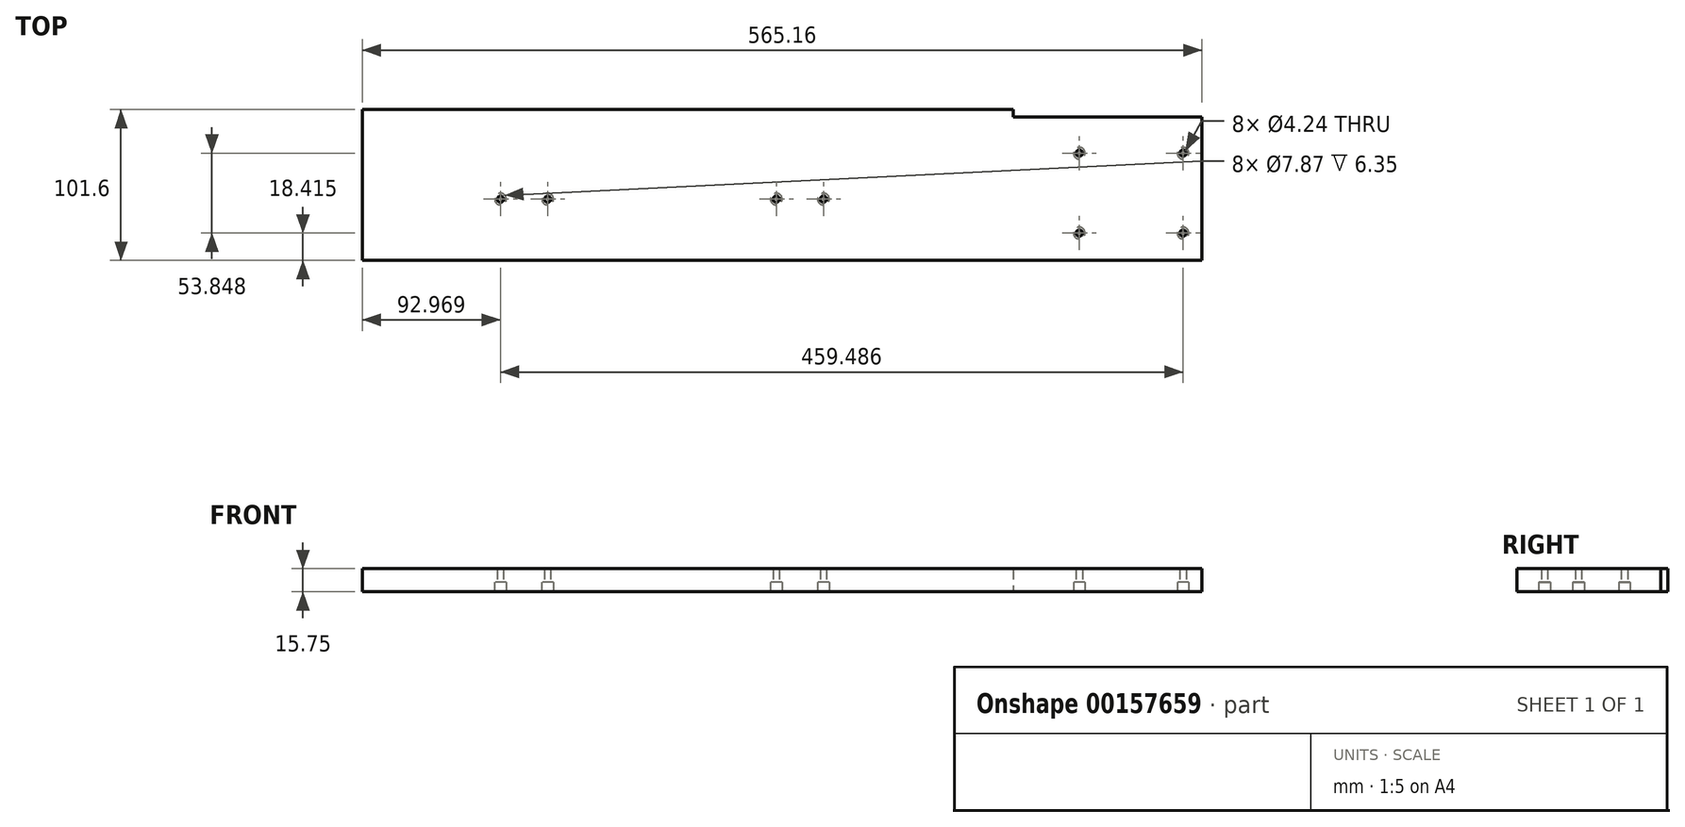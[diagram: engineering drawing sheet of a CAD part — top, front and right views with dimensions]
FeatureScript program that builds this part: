
annotation { "Feature Type Name" : "Feature", "Feature Type Description" : "" }
export const myFeature = defineFeature(function(context is Context, id is Id, definition is map)
    precondition{}
    {
        {
            var Q0;
            Q0=qCreatedBy(makeId("Top.planeOp"),FACE);
            var sketch = newSketch(context, id + "F0", { "sketchPlane" : qUnion([Q0])});
            skLineSegment(sketch, "E0.bottom", {"start": v(282.58, -50.8) * mm, "end": v(-282.58, -50.8) * mm});
            skLineSegment(sketch, "E0.top", {"start": v(155.58, 50.8) * mm, "end": v(-282.58, 50.8) * mm});
            skLineSegment(sketch, "E0.left", {"start": v(282.58, -50.8) * mm, "end": v(282.58, 45.97) * mm});
            skLineSegment(sketch, "E0.right", {"start": v(-282.58, -50.8) * mm, "end": v(-282.58, 50.8) * mm});
            skPoint(sketch, "E0.middle", {"position": v(0, 0) * mm});
            skLineSegment(sketch, "E1.bottom", {"start": v(269.88, -32.38) * mm, "end": v(200.03, -32.38) * mm, "construction": true});
            skLineSegment(sketch, "E1.top", {"start": v(269.88, 21.46) * mm, "end": v(200.03, 21.46) * mm, "construction": true});
            skLineSegment(sketch, "E1.left", {"start": v(269.88, -32.38) * mm, "end": v(269.88, 21.46) * mm, "construction": true});
            skLineSegment(sketch, "E1.right", {"start": v(200.03, -32.38) * mm, "end": v(200.03, 21.46) * mm, "construction": true});
            skPoint(sketch, "E1.middle", {"position": v(234.95, -5.46) * mm});
            skCircle(sketch, "E2", {"center": v(200.03, 21.46) * mm, "radius": 2.12 * mm});
            skCircle(sketch, "E3", {"center": v(269.88, 21.46) * mm, "radius": 2.12 * mm});
            skCircle(sketch, "E4", {"center": v(200.03, -32.38) * mm, "radius": 2.12 * mm});
            skCircle(sketch, "E5", {"center": v(269.88, -32.38) * mm, "radius": 2.12 * mm});
            skCircle(sketch, "E6", {"center": v(200.03, 21.46) * mm, "radius": 3.94 * mm});
            skCircle(sketch, "E7", {"center": v(269.88, 21.46) * mm, "radius": 3.94 * mm});
            skCircle(sketch, "E8", {"center": v(269.88, -32.38) * mm, "radius": 3.94 * mm});
            skCircle(sketch, "E9", {"center": v(200.03, -32.38) * mm, "radius": 3.94 * mm});
            skCircle(sketch, "E10", {"center": v(27.81, -9.52) * mm, "radius": 2.12 * mm});
            skCircle(sketch, "E11", {"center": v(-3.94, -9.53) * mm, "radius": 2.12 * mm});
            skCircle(sketch, "E12", {"center": v(-157.86, -9.53) * mm, "radius": 2.12 * mm});
            skCircle(sketch, "E13", {"center": v(-189.61, -9.53) * mm, "radius": 2.12 * mm});
            skCircle(sketch, "E14", {"center": v(27.81, -9.52) * mm, "radius": 3.94 * mm});
            skCircle(sketch, "E15", {"center": v(-3.94, -9.53) * mm, "radius": 3.94 * mm});
            skCircle(sketch, "E16", {"center": v(-157.86, -9.53) * mm, "radius": 3.94 * mm});
            skCircle(sketch, "E17", {"center": v(-189.61, -9.53) * mm, "radius": 3.94 * mm});
            skLineSegment(sketch, "E18.top", {"start": v(282.58, 45.97) * mm, "end": v(155.58, 45.97) * mm, "construction": true});
            skLineSegment(sketch, "E18.right", {"start": v(155.58, 50.8) * mm, "end": v(155.58, 45.97) * mm, "construction": true});
            skLineSegment(sketch, "E19", {"start": v(155.58, 45.97) * mm, "end": v(282.58, 45.97) * mm, "construction": true});
            skLineSegment(sketch, "E20", {"start": v(282.58, 45.97) * mm, "end": v(155.58, 45.97) * mm});
            skLineSegment(sketch, "E21", {"start": v(155.58, 50.8) * mm, "end": v(155.58, 45.97) * mm});
            skSolve(sketch);
        }
        {
            var Q0;
            Q0=makeQuery(id+"F0.imprint","IMPRINT",FACE,{"disambiguationData":[TD([[makeQuery(id+"F0.imprint","IMPRINT",EDGE,{"derivedFrom":sQuery(id+"F0.wireOp",EDGE,"E2")}),-1.0]])]});
            var Q1;
            Q1=makeQuery(id+"F0.imprint","IMPRINT",FACE,{"disambiguationData":[TD([[makeQuery(id+"F0.imprint","IMPRINT",EDGE,{"derivedFrom":sQuery(id+"F0.wireOp",EDGE,"E4")}),-1.0]])]});
            var Q2;
            Q2=makeQuery(id+"F0.imprint","IMPRINT",FACE,{"disambiguationData":[TD([[makeQuery(id+"F0.imprint","IMPRINT",EDGE,{"derivedFrom":sQuery(id+"F0.wireOp",EDGE,"E5")}),-1.0]])]});
            var Q3;
            Q3=makeQuery(id+"F0.imprint","IMPRINT",FACE,{"disambiguationData":[TD([[makeQuery(id+"F0.imprint","IMPRINT",EDGE,{"derivedFrom":sQuery(id+"F0.wireOp",EDGE,"E3")}),-1.0]])]});
            var Q4;
            Q4=makeQuery(id+"F0.imprint","IMPRINT",FACE,{"disambiguationData":[TD([[makeQuery(id+"F0.imprint","IMPRINT",EDGE,{"derivedFrom":sQuery(id+"F0.wireOp",EDGE,"E10")}),-1.0]])]});
            var Q5;
            Q5=makeQuery(id+"F0.imprint","IMPRINT",FACE,{"disambiguationData":[TD([[makeQuery(id+"F0.imprint","IMPRINT",EDGE,{"derivedFrom":sQuery(id+"F0.wireOp",EDGE,"E11")}),-1.0]])]});
            var Q6;
            Q6=makeQuery(id+"F0.imprint","IMPRINT",FACE,{"disambiguationData":[TD([[makeQuery(id+"F0.imprint","IMPRINT",EDGE,{"derivedFrom":sQuery(id+"F0.wireOp",EDGE,"E12")}),-1.0]])]});
            var Q7;
            Q7=makeQuery(id+"F0.imprint","IMPRINT",FACE,{"disambiguationData":[TD([[makeQuery(id+"F0.imprint","IMPRINT",EDGE,{"derivedFrom":sQuery(id+"F0.wireOp",EDGE,"E13")}),-1.0]])]});
            var Q8;
            Q8=makeQuery(id+"F0.imprint","IMPRINT",FACE,{"disambiguationData":[TD([[makeQuery(id+"F0.imprint","IMPRINT",EDGE,{"derivedFrom":sQuery(id+"F0.wireOp",EDGE,"E0.bottom")}),-1.0]])]});
            extrude(context, id + "F1", {"entities" : qUnion([Q0, Q1, Q2, Q3, Q4, Q5, Q6, Q7, Q8]), "depth" : 15.75 * mm});
        }
        {
            var Q0;
            Q0=makeQuery(id+"F0.imprint","IMPRINT",FACE,{"disambiguationData":[TD([[makeQuery(id+"F0.imprint","IMPRINT",EDGE,{"derivedFrom":sQuery(id+"F0.wireOp",EDGE,"E13")}),-1.0]])]});
            var Q1;
            Q1=makeQuery(id+"F0.imprint","IMPRINT",FACE,{"disambiguationData":[TD([[makeQuery(id+"F0.imprint","IMPRINT",EDGE,{"derivedFrom":sQuery(id+"F0.wireOp",EDGE,"E12")}),-1.0]])]});
            var Q2;
            Q2=makeQuery(id+"F0.imprint","IMPRINT",FACE,{"disambiguationData":[TD([[makeQuery(id+"F0.imprint","IMPRINT",EDGE,{"derivedFrom":sQuery(id+"F0.wireOp",EDGE,"E11")}),-1.0]])]});
            var Q3;
            Q3=makeQuery(id+"F0.imprint","IMPRINT",FACE,{"disambiguationData":[TD([[makeQuery(id+"F0.imprint","IMPRINT",EDGE,{"derivedFrom":sQuery(id+"F0.wireOp",EDGE,"E10")}),-1.0]])]});
            var Q4;
            Q4=makeQuery(id+"F0.imprint","IMPRINT",FACE,{"disambiguationData":[TD([[makeQuery(id+"F0.imprint","IMPRINT",EDGE,{"derivedFrom":sQuery(id+"F0.wireOp",EDGE,"E2")}),-1.0]])]});
            var Q5;
            Q5=makeQuery(id+"F0.imprint","IMPRINT",FACE,{"disambiguationData":[TD([[makeQuery(id+"F0.imprint","IMPRINT",EDGE,{"derivedFrom":sQuery(id+"F0.wireOp",EDGE,"E3")}),-1.0]])]});
            var Q6;
            Q6=makeQuery(id+"F0.imprint","IMPRINT",FACE,{"disambiguationData":[TD([[makeQuery(id+"F0.imprint","IMPRINT",EDGE,{"derivedFrom":sQuery(id+"F0.wireOp",EDGE,"E5")}),-1.0]])]});
            var Q7;
            Q7=makeQuery(id+"F0.imprint","IMPRINT",FACE,{"disambiguationData":[TD([[makeQuery(id+"F0.imprint","IMPRINT",EDGE,{"derivedFrom":sQuery(id+"F0.wireOp",EDGE,"E4")}),-1.0]])]});
            extrude(context, id + "F2", {"entities" : qUnion([Q0, Q1, Q2, Q3, Q4, Q5, Q6, Q7]), "operationType" : NewBodyOperationType.REMOVE, "depth" : 6.35 * mm});
        }
    });
